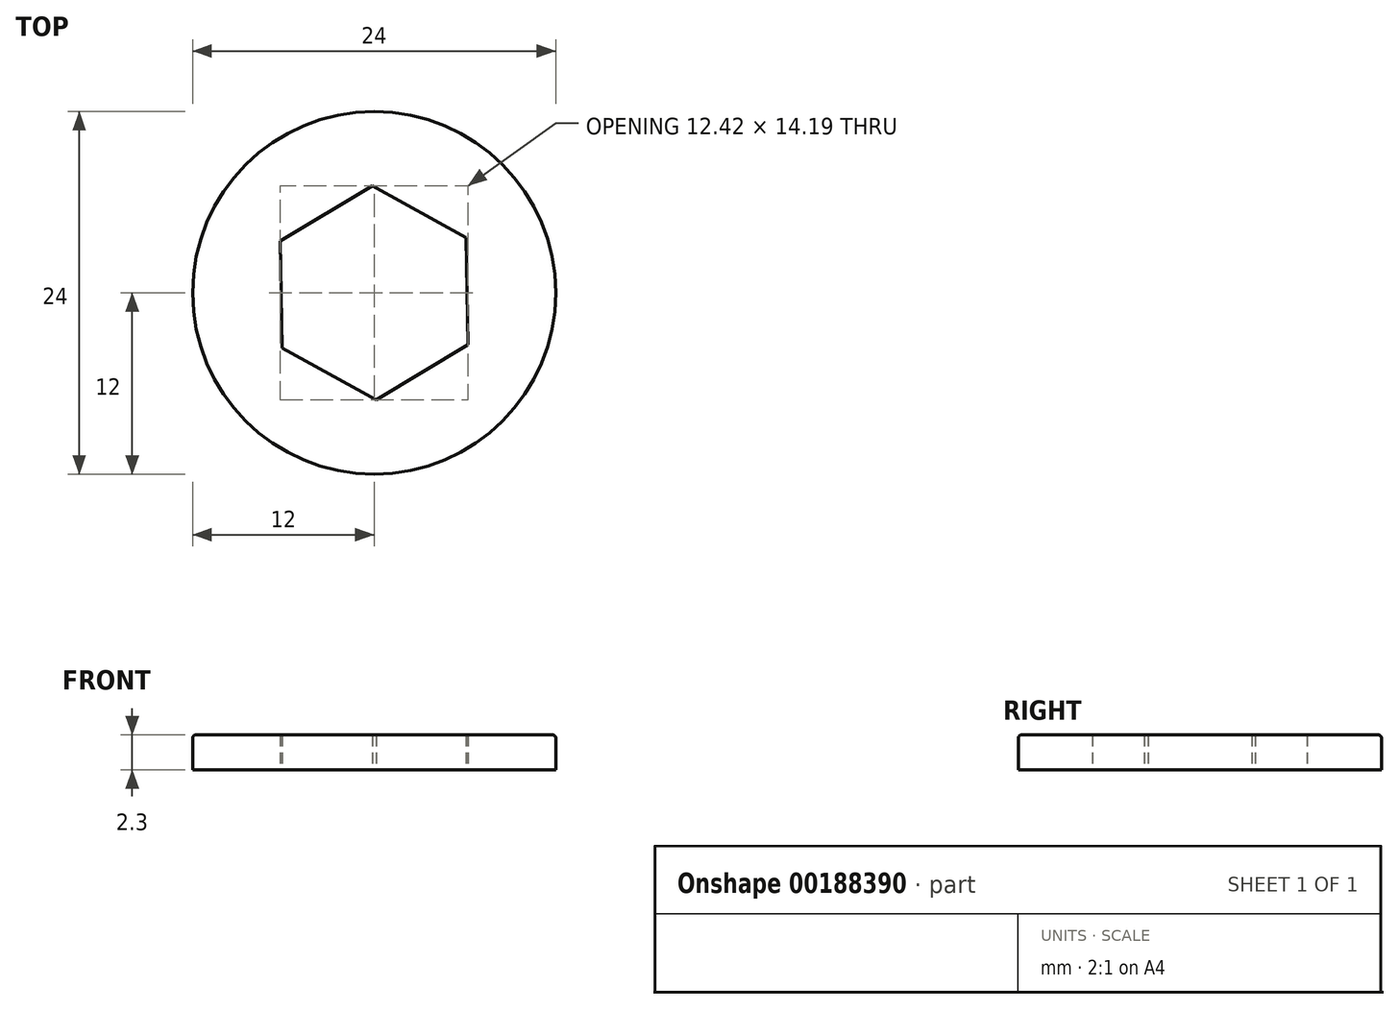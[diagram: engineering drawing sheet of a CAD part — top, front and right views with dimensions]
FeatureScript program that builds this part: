
annotation { "Feature Type Name" : "Feature", "Feature Type Description" : "" }
export const myFeature = defineFeature(function(context is Context, id is Id, definition is map)
    precondition{}
    {
        {
            var Q0;
            Q0=qCreatedBy(makeId("Top.planeOp"),FACE);
            var sketch = newSketch(context, id + "F0", { "sketchPlane" : qUnion([Q0])});
            skCircle(sketch, "E0", {"center": v(0, 0) * mm, "radius": 12 * mm});
            skCircle(sketch, "E1.cCircle", {"center": v(0, 0) * mm, "radius": 7.1 * mm, "construction": true});
            skLineSegment(sketch, "E1.0", {"start": v(6.2, -3.43) * mm, "end": v(0.13, -7.1) * mm});
            skLineSegment(sketch, "E1.1", {"start": v(0.13, -7.1) * mm, "end": v(-6.08, -3.66) * mm});
            skLineSegment(sketch, "E1.2", {"start": v(-6.08, -3.66) * mm, "end": v(-6.2, 3.43) * mm});
            skLineSegment(sketch, "E1.3", {"start": v(-6.2, 3.43) * mm, "end": v(-0.13, 7.1) * mm});
            skLineSegment(sketch, "E1.4", {"start": v(-0.13, 7.1) * mm, "end": v(6.08, 3.66) * mm});
            skLineSegment(sketch, "E1.5", {"start": v(6.08, 3.66) * mm, "end": v(6.2, -3.43) * mm});
            skSolve(sketch);
        }
        {
            var Q0;
            Q0=makeQuery(id+"F0.imprint","IMPRINT",FACE,{"disambiguationData":[TD([[makeQuery(id+"F0.imprint","IMPRINT",EDGE,{"derivedFrom":sQuery(id+"F0.wireOp",EDGE,"E0")}),1.0]])]});
            extrude(context, id + "F1", {"entities" : qUnion([Q0]), "depth" : 2.3 * mm});
        }
        {
            var Q0;
            Q0=makeQuery(id+"F1.opExtrude","CAP_EDGE",EDGE,{"disambiguationData":[OSD([sQuery(id+"F0.wireOp",EDGE,"E0")])],"isStart":false});
            fillet(context, id + "F2", {"entities" : qUnion([Q0]), "radius" : 0.2 * mm, "tangentPropagation" : true, "allowEdgeOverflow" : false});
        }
    });
